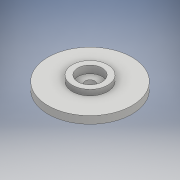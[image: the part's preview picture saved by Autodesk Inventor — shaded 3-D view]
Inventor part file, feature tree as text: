
AUTODESK INVENTOR PART (.ipt)
format: ipt  version: 2017 (Build 210142000, 142)  size: 176,128 bytes
history: native  units: mm
features: sketch x5, extrude x4, revolve x1
ambient origin geometry x8: Origin, YZ Plane, XZ Plane, XY Plane, X Axis, Y Axis, Z Axis, Center Point
bodies: Body1 (feature_tree)
feature tree (10):
  revolve  "Revolution2"  [1 undecoded]
  extrude  "Extrusion6"  Depth=7.0mm
  extrude  "Extrusion7"  Depth=4.0mm
  extrude  "Extrusion8"  Depth=4.0mm
  extrude  "Extrusion9"  Depth=4.0mm
  sketch  "Sketch1"  dims[d1=2.5mm d2=4.0mm]
  sketch  "Sketch6"  dims[d3=7.0mm d4=20.0mm]
  sketch  "Sketch7"  dims[d5=34.0mm d9=4.0mm]
  sketch  "Sketch8"  dims[d12=2.5mm d13=4.0mm]
  sketch  "Sketch9"  dims[d55=22.5mm d56=4.0mm d57=90.0deg d64=20.0mm d65=90.0deg d69=15.0mm d71=15.0mm d73=5.0mm d74=0.0mm d75=2.5mm d76=5.0mm d77=5.0mm d78=26.0mm d79=0.0mm d80=3.0mm d81=3.0mm d82=3.0mm d83=3.0mm d84=4.0mm d85=0.0mm d86=100.0mm d87=0.0mm]
note: 1 required parameter value undecoded (feature->parameter linkage not recoverable at this tier; creation-order binding heuristic only, values carry confidence <= 0.55)
